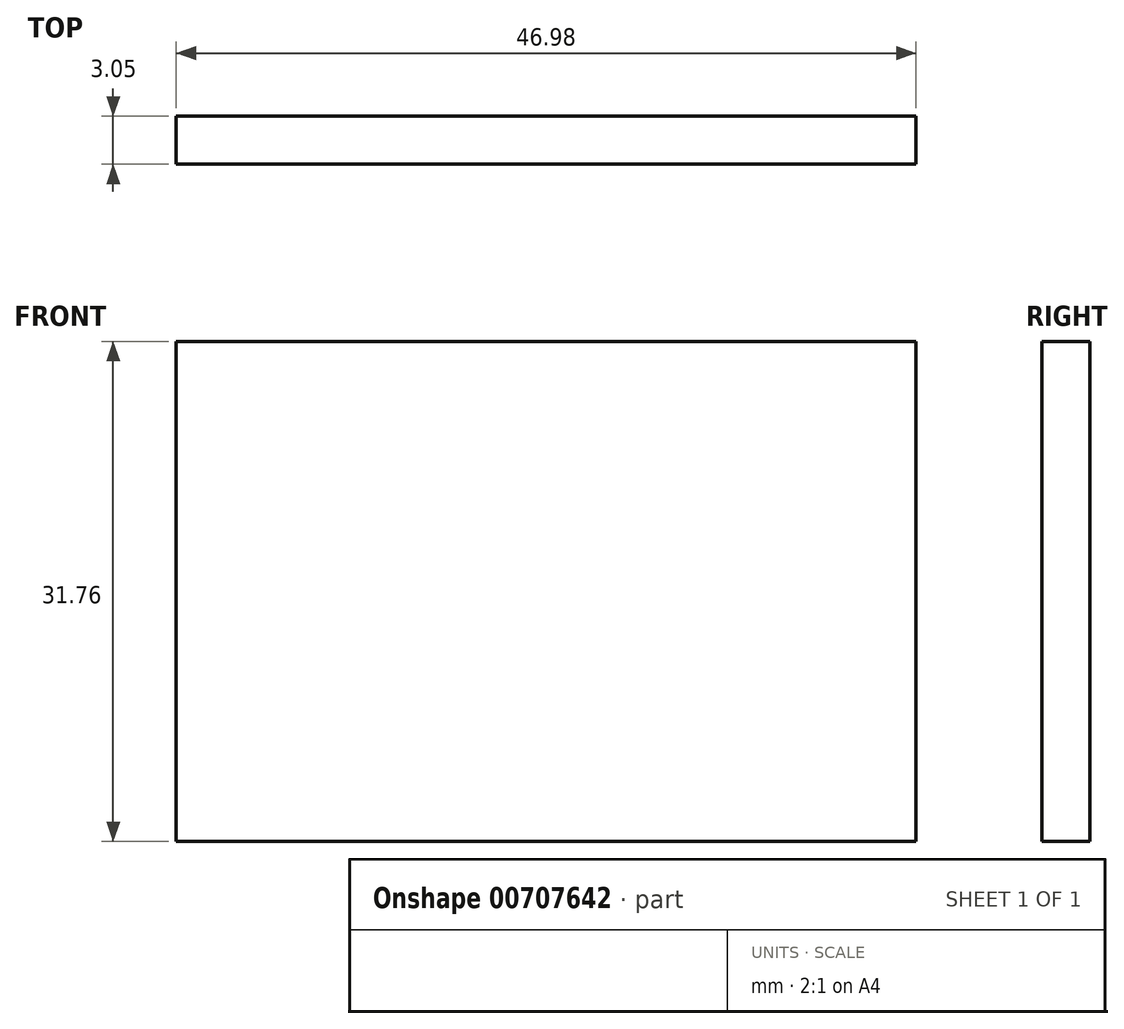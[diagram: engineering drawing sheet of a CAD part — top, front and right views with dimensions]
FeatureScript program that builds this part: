
annotation { "Feature Type Name" : "Feature", "Feature Type Description" : "" }
export const myFeature = defineFeature(function(context is Context, id is Id, definition is map)
    precondition{}
    {
        {
            var Q0;
            Q0=qCreatedBy(makeId("Front.planeOp"),FACE);
            var sketch = newSketch(context, id + "F0", { "sketchPlane" : qUnion([Q0])});
            skLineSegment(sketch, "E0.bottom", {"start": v(23.5, 15.88) * mm, "end": v(-23.5, 15.88) * mm});
            skLineSegment(sketch, "E0.top", {"start": v(23.5, -15.88) * mm, "end": v(-23.5, -15.88) * mm});
            skLineSegment(sketch, "E0.left", {"start": v(23.5, 15.88) * mm, "end": v(23.5, -15.88) * mm});
            skLineSegment(sketch, "E0.right", {"start": v(-23.5, 15.88) * mm, "end": v(-23.5, -15.88) * mm});
            skPoint(sketch, "E0.middle", {"position": v(0, 0) * mm});
            skSolve(sketch);
        }
        {
            var Q0;
            Q0=qSketchRegion(id+"F0",true);
            extrude(context, id + "F1", {"entities" : qUnion([Q0]), "depth" : 3.05 * mm, "offsetDistance" : 25.4 * mm});
        }
    });
